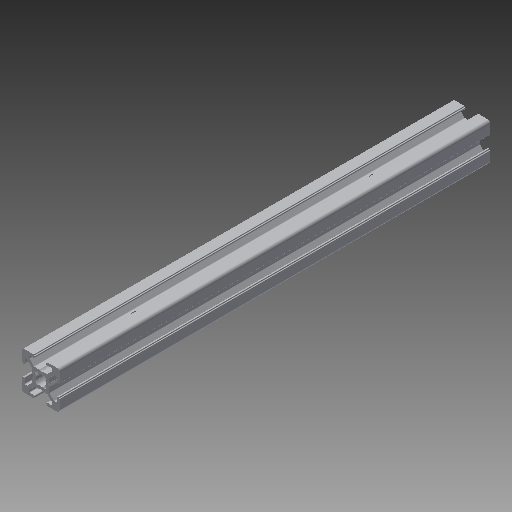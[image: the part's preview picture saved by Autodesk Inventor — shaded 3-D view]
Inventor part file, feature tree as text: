
AUTODESK INVENTOR PART (.ipt)
format: ipt  version: 2017 (Build 210142000, 142)  size: 406,528 bytes
history: native  units: in
note: dims shown in document units (in); Inventor stores cm internally (conversion verified against a paired STEP export)
features: other x3, sketch x2, extrude x1, hole x1, mirror x1
ambient origin geometry x8: Origin, YZ Plane, XZ Plane, XY Plane, X Axis, Y Axis, Z Axis, Center Point
bodies: Solid1 (feature_tree)
feature tree (8):
  other  "Blocks"
  extrude  "Extrusion1"  Depth=2.0in
  hole  "Hole1"  [1 undecoded]
  mirror  "Mirror1"
  sketch  "Sketch1"  dims[d1=0.0in d5=2.0in]
  other  "20x20"
  sketch  "Sketch3"  dims[d6=0.187in d7=0.75in d8=0.375in d9=0.25in d10=0.5635in d11=1.0in d12=0.8108in d13=1.0in d14=1.0in]
  other  "20x20:1"
note: 1 required parameter value undecoded (feature->parameter linkage not recoverable at this tier; creation-order binding heuristic only, values carry confidence <= 0.55)
